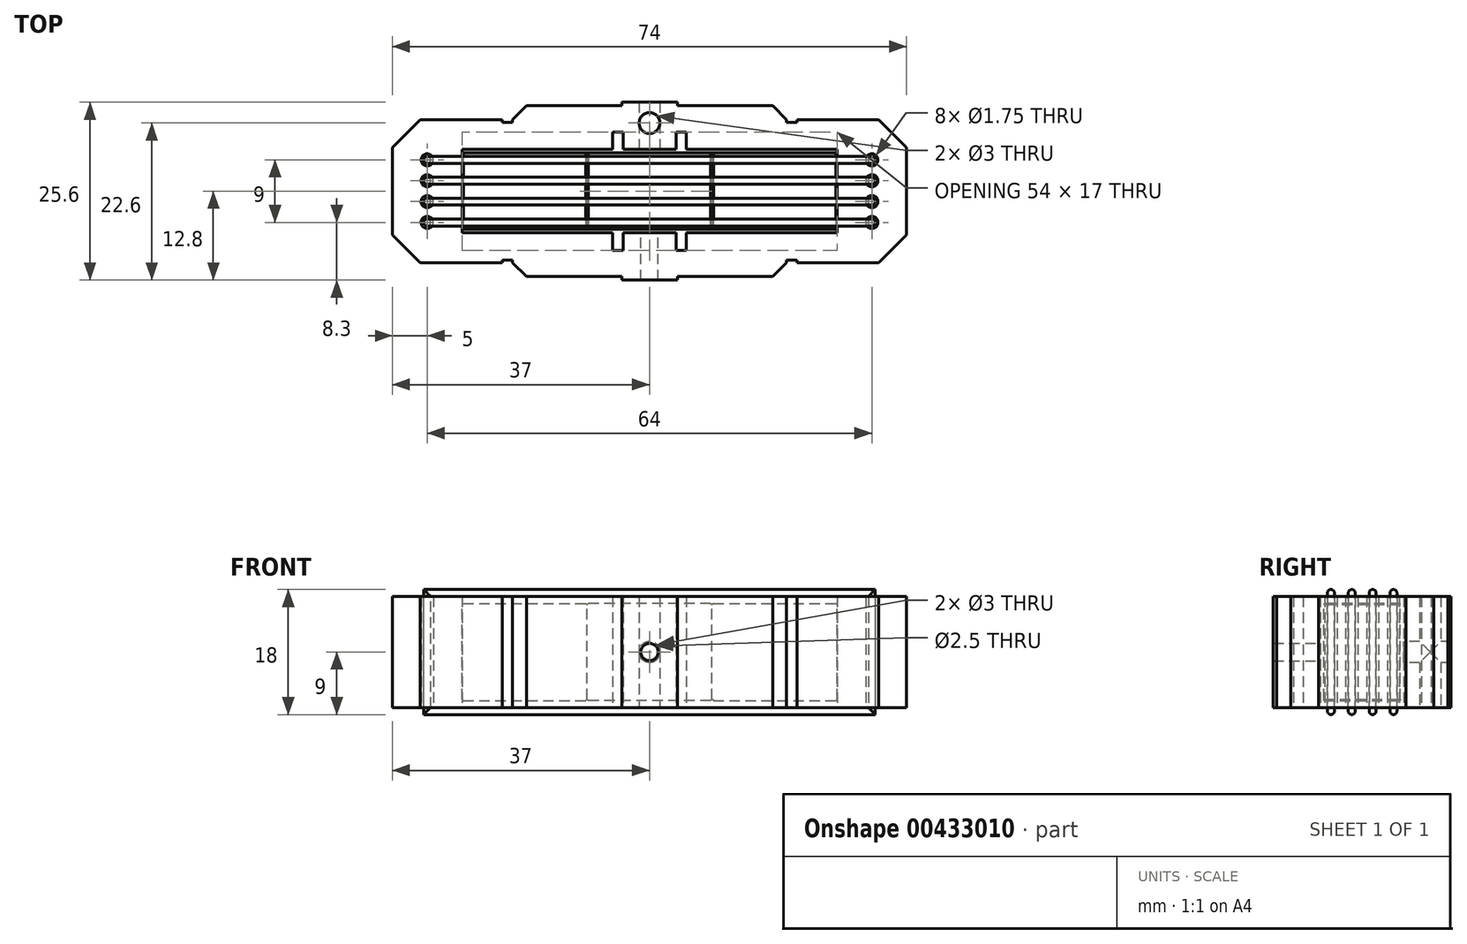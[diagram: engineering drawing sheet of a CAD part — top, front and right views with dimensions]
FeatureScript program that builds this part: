
annotation { "Feature Type Name" : "Feature", "Feature Type Description" : "" }
export const myFeature = defineFeature(function(context is Context, id is Id, definition is map)
    precondition{}
    {
        {
            var Q0;
            Q0=qCreatedBy(makeId("Top.planeOp"),FACE);
            var sketch = newSketch(context, id + "F0", { "sketchPlane" : qUnion([Q0])});
            skLineSegment(sketch, "E0", {"start": v(0, 12.8) * mm, "end": v(4, 12.8) * mm});
            skLineSegment(sketch, "E1", {"start": v(4, 12.8) * mm, "end": v(4, 12.3) * mm});
            skLineSegment(sketch, "E2", {"start": v(4, 12.3) * mm, "end": v(17.72, 12.3) * mm});
            skLineSegment(sketch, "E3", {"start": v(19.72, 9.92) * mm, "end": v(21.22, 9.92) * mm});
            skLineSegment(sketch, "E4", {"start": v(21.22, 9.92) * mm, "end": v(21.22, 10.3) * mm});
            skLineSegment(sketch, "E5", {"start": v(21.22, 10.3) * mm, "end": v(33, 10.3) * mm});
            skLineSegment(sketch, "E6", {"start": v(33, 10.3) * mm, "end": v(37, 6.3) * mm});
            skLineSegment(sketch, "E7", {"start": v(37, 6.3) * mm, "end": v(37, 0) * mm});
            skLineSegment(sketch, "E8", {"start": v(17.72, 12.3) * mm, "end": v(19.72, 10.3) * mm});
            skLineSegment(sketch, "E9", {"start": v(19.72, 10.3) * mm, "end": v(19.72, 9.92) * mm});
            skLineSegment(sketch, "E10", {"start": v(37, 0) * mm, "end": v(27, 0) * mm});
            skLineSegment(sketch, "E11", {"start": v(27, 0) * mm, "end": v(27, 6) * mm});
            skLineSegment(sketch, "E12", {"start": v(0, 6) * mm, "end": v(0, 12.8) * mm});
            skLineSegment(sketch, "E13", {"start": v(27, 6) * mm, "end": v(5.3, 6) * mm});
            skLineSegment(sketch, "E14", {"start": v(5.3, 6) * mm, "end": v(5.3, 8.5) * mm});
            skLineSegment(sketch, "E15", {"start": v(5.3, 8.5) * mm, "end": v(3.8, 8.5) * mm});
            skLineSegment(sketch, "E16", {"start": v(3.8, 8.5) * mm, "end": v(3.8, 6) * mm});
            skLineSegment(sketch, "E17", {"start": v(3.8, 6) * mm, "end": v(0, 6) * mm});
            skPoint(sketch, "E18", {"position": v(32, 4.5) * mm});
            skPoint(sketch, "E19", {"position": v(32, 1.5) * mm});
            skCircle(sketch, "E20", {"center": v(32, 1.5) * mm, "radius": 0.88 * mm});
            skCircle(sketch, "E21", {"center": v(32, 4.5) * mm, "radius": 0.88 * mm});
            skSolve(sketch);
        }
        {
            var Q0;
            Q0 = qSketchRegion(id + "F0", true);
            extrude(context, id + "F1", {"entities" : qUnion([Q0]), "depth" : 16 * mm, "symmetric" : true});
        }
        {
            var Q0;
            Q0=makeQuery(id+"F1.opExtrude","SWEPT_BODY",BODY,{"disambiguationData":[OSD([sQuery(id+"F0.wireOp",EDGE,"E0"),sQuery(id+"F0.wireOp",EDGE,"E1"),sQuery(id+"F0.wireOp",EDGE,"E2"),sQuery(id+"F0.wireOp",EDGE,"E3"),sQuery(id+"F0.wireOp",EDGE,"E4"),sQuery(id+"F0.wireOp",EDGE,"E5"),sQuery(id+"F0.wireOp",EDGE,"E6"),sQuery(id+"F0.wireOp",EDGE,"E7"),sQuery(id+"F0.wireOp",EDGE,"E8"),sQuery(id+"F0.wireOp",EDGE,"E9"),sQuery(id+"F0.wireOp",EDGE,"E10"),sQuery(id+"F0.wireOp",EDGE,"E11"),sQuery(id+"F0.wireOp",EDGE,"GGBhrQa4-wOD3-Jy7S-9Qvg-qyJeMn5F3UjZ"),sQuery(id+"F0.wireOp",EDGE,"E12")])]});
            var Q1;
            Q1=qCreatedBy(makeId("Front.planeOp"),FACE);
            mirror(context, id + "F2", {"operationType" : NewBodyOperationType.ADD, "entities" : qUnion([Q0]), "mirrorPlane" : qUnion([Q1])});
        }
        {
            var Q0;
            Q0=makeQuery(id+"F1.opExtrude","SWEPT_BODY",BODY,{"disambiguationData":[OSD([sQuery(id+"F0.wireOp",EDGE,"E0"),sQuery(id+"F0.wireOp",EDGE,"E1"),sQuery(id+"F0.wireOp",EDGE,"E2"),sQuery(id+"F0.wireOp",EDGE,"E3"),sQuery(id+"F0.wireOp",EDGE,"E4"),sQuery(id+"F0.wireOp",EDGE,"E5"),sQuery(id+"F0.wireOp",EDGE,"E6"),sQuery(id+"F0.wireOp",EDGE,"E7"),sQuery(id+"F0.wireOp",EDGE,"E8"),sQuery(id+"F0.wireOp",EDGE,"E9"),sQuery(id+"F0.wireOp",EDGE,"E10"),sQuery(id+"F0.wireOp",EDGE,"E11"),sQuery(id+"F0.wireOp",EDGE,"GGBhrQa4-wOD3-Jy7S-9Qvg-qyJeMn5F3UjZ"),sQuery(id+"F0.wireOp",EDGE,"E12")])]});
            var Q1;
            Q1=qCreatedBy(makeId("Right.planeOp"),FACE);
            mirror(context, id + "F3", {"operationType" : NewBodyOperationType.ADD, "entities" : qUnion([Q0]), "mirrorPlane" : qUnion([Q1])});
        }
        {
            var Q0;
            {var subQ0=makeQuery(id+"F1.opExtrude","CAP_FACE",FACE,{"disambiguationData":[OSD([sQuery(id+"F0.wireOp",EDGE,"E0"),sQuery(id+"F0.wireOp",EDGE,"E1"),sQuery(id+"F0.wireOp",EDGE,"E2"),sQuery(id+"F0.wireOp",EDGE,"E3"),sQuery(id+"F0.wireOp",EDGE,"E4"),sQuery(id+"F0.wireOp",EDGE,"E5"),sQuery(id+"F0.wireOp",EDGE,"E6"),sQuery(id+"F0.wireOp",EDGE,"E7"),sQuery(id+"F0.wireOp",EDGE,"E8"),sQuery(id+"F0.wireOp",EDGE,"E9"),sQuery(id+"F0.wireOp",EDGE,"E10"),sQuery(id+"F0.wireOp",EDGE,"E11"),sQuery(id+"F0.wireOp",EDGE,"E12"),sQuery(id+"F0.wireOp",EDGE,"E13"),sQuery(id+"F0.wireOp",EDGE,"E14"),sQuery(id+"F0.wireOp",EDGE,"E15"),sQuery(id+"F0.wireOp",EDGE,"E16"),sQuery(id+"F0.wireOp",EDGE,"E17")])],"isStart":false});var subQ1=makeQuery(id+"F2.boolean.opBoolean","MERGE",FACE,{"derivedFrom":[subQ0,makeQuery(id+"F2.opPattern","COPY",FACE,{"derivedFrom":subQ0,"instanceName":"1"})]});Q0=makeQuery(id+"F3.boolean.opBoolean","MERGE",FACE,{"derivedFrom":[subQ1,makeQuery(id+"F3.opPattern","COPY",FACE,{"derivedFrom":subQ1,"instanceName":"1"})]});}
            var sketch = newSketch(context, id + "F4", { "sketchPlane" : qUnion([Q0])});
            skPoint(sketch, "E22", {"position": v(0, 9.8) * mm});
            skSolve(sketch);
        }
        {
            var Q0;
            Q0=sQuery(id+"F4.wireOp",VERTEX,"E22");
            var Q1;
            Q1=makeQuery(id+"F1.opExtrude","SWEPT_BODY",BODY,{"disambiguationData":[OSD([sQuery(id+"F0.wireOp",EDGE,"E0"),sQuery(id+"F0.wireOp",EDGE,"E1"),sQuery(id+"F0.wireOp",EDGE,"E2"),sQuery(id+"F0.wireOp",EDGE,"E3"),sQuery(id+"F0.wireOp",EDGE,"E4"),sQuery(id+"F0.wireOp",EDGE,"E5"),sQuery(id+"F0.wireOp",EDGE,"E6"),sQuery(id+"F0.wireOp",EDGE,"E7"),sQuery(id+"F0.wireOp",EDGE,"E8"),sQuery(id+"F0.wireOp",EDGE,"E9"),sQuery(id+"F0.wireOp",EDGE,"E10"),sQuery(id+"F0.wireOp",EDGE,"E11"),sQuery(id+"F0.wireOp",EDGE,"E12"),sQuery(id+"F0.wireOp",EDGE,"E13"),sQuery(id+"F0.wireOp",EDGE,"E14"),sQuery(id+"F0.wireOp",EDGE,"E15"),sQuery(id+"F0.wireOp",EDGE,"E16"),sQuery(id+"F0.wireOp",EDGE,"E17")])]});
            hole(context, id + "F5", {"style" : HoleStyle.SIMPLE, "endStyle" : HoleEndStyle.THROUGH, "holeDiameter" : 3 * mm, "tappedDepth" : 12 * mm, "tapClearance" : 3, "locations" : qUnion([Q0]), "scope" : qUnion([Q1]), "startStyle" : HoleStartStyle.PART});
        }
        {
            var Q0;
            {var subQ0=makeQuery(id+"F2.opPattern","COPY",FACE,{"derivedFrom":makeQuery(id+"F1.opExtrude","SWEPT_FACE",FACE,{"disambiguationData":[OSD([sQuery(id+"F0.wireOp",EDGE,"E0")])]}),"instanceName":"1"});Q0=makeQuery(id+"F3.boolean.opBoolean","MERGE",FACE,{"derivedFrom":[subQ0,makeQuery(id+"F3.opPattern","COPY",FACE,{"derivedFrom":subQ0,"instanceName":"1"})]});}
            var sketch = newSketch(context, id + "F6", { "sketchPlane" : qUnion([Q0])});
            skPoint(sketch, "E23", {"position": v(0, 0) * mm});
            skSolve(sketch);
        }
        {
            var Q0;
            Q0=sQuery(id+"F6.wireOp",VERTEX,"E23");
            var Q1;
            Q1=makeQuery(id+"F1.opExtrude","SWEPT_BODY",BODY,{"disambiguationData":[OSD([sQuery(id+"F0.wireOp",EDGE,"E0"),sQuery(id+"F0.wireOp",EDGE,"E1"),sQuery(id+"F0.wireOp",EDGE,"E2"),sQuery(id+"F0.wireOp",EDGE,"E3"),sQuery(id+"F0.wireOp",EDGE,"E4"),sQuery(id+"F0.wireOp",EDGE,"E5"),sQuery(id+"F0.wireOp",EDGE,"E6"),sQuery(id+"F0.wireOp",EDGE,"E7"),sQuery(id+"F0.wireOp",EDGE,"E8"),sQuery(id+"F0.wireOp",EDGE,"E9"),sQuery(id+"F0.wireOp",EDGE,"E10"),sQuery(id+"F0.wireOp",EDGE,"E11"),sQuery(id+"F0.wireOp",EDGE,"E12"),sQuery(id+"F0.wireOp",EDGE,"E13"),sQuery(id+"F0.wireOp",EDGE,"E14"),sQuery(id+"F0.wireOp",EDGE,"E15"),sQuery(id+"F0.wireOp",EDGE,"E16"),sQuery(id+"F0.wireOp",EDGE,"E17"),sQuery(id+"F0.wireOp",EDGE,"E20"),sQuery(id+"F0.wireOp",EDGE,"E21")])]});
            hole(context, id + "F7", {"style" : HoleStyle.SIMPLE, "endStyle" : HoleEndStyle.BLIND, "standardTappedOrClearance" : lookupTablePath({ "standard" : "ISO", "engagement" : "75%", "pitch" : "0.5 mm", "size" : "M3", "type" : "Tapped" }), "standardBlindInLast" : lookupTablePath({ "standard" : "ISO", "engagement" : "75%", "pitch" : "0.5 mm", "size" : "M3", "type" : "Tapped" }), "holeDiameter" : 2.5 * mm, "showTappedDepth" : true, "holeDepth" : 13.5 * mm, "tappedDepth" : 12 * mm, "tapClearance" : 3, "locations" : qUnion([Q0]), "scope" : qUnion([Q1]), "majorDiameter" : 3 * mm, "startStyle" : HoleStartStyle.PART});
        }
        {
            var Q0;
            {var subQ0=makeQuery(id+"F1.opExtrude","SWEPT_FACE",FACE,{"disambiguationData":[OSD([sQuery(id+"F0.wireOp",EDGE,"E0")])]});Q0=makeQuery(id+"F3.boolean.opBoolean","MERGE",FACE,{"derivedFrom":[subQ0,makeQuery(id+"F3.opPattern","COPY",FACE,{"derivedFrom":subQ0,"instanceName":"1"})]});}
            var sketch = newSketch(context, id + "F8", { "sketchPlane" : qUnion([Q0])});
            skPoint(sketch, "E24", {"position": v(0, 0) * mm});
            skSolve(sketch);
        }
        {
            var Q0;
            Q0=sQuery(id+"F8.wireOp",VERTEX,"E24");
            var Q1;
            Q1=makeQuery(id+"F1.opExtrude","SWEPT_BODY",BODY,{"disambiguationData":[OSD([sQuery(id+"F0.wireOp",EDGE,"E0"),sQuery(id+"F0.wireOp",EDGE,"E1"),sQuery(id+"F0.wireOp",EDGE,"E2"),sQuery(id+"F0.wireOp",EDGE,"E3"),sQuery(id+"F0.wireOp",EDGE,"E4"),sQuery(id+"F0.wireOp",EDGE,"E5"),sQuery(id+"F0.wireOp",EDGE,"E6"),sQuery(id+"F0.wireOp",EDGE,"E7"),sQuery(id+"F0.wireOp",EDGE,"E8"),sQuery(id+"F0.wireOp",EDGE,"E9"),sQuery(id+"F0.wireOp",EDGE,"E10"),sQuery(id+"F0.wireOp",EDGE,"E11"),sQuery(id+"F0.wireOp",EDGE,"E12"),sQuery(id+"F0.wireOp",EDGE,"E13"),sQuery(id+"F0.wireOp",EDGE,"E14"),sQuery(id+"F0.wireOp",EDGE,"E15"),sQuery(id+"F0.wireOp",EDGE,"E16"),sQuery(id+"F0.wireOp",EDGE,"E17"),sQuery(id+"F0.wireOp",EDGE,"E20"),sQuery(id+"F0.wireOp",EDGE,"E21")])]});
            hole(context, id + "F9", {"style" : HoleStyle.SIMPLE, "endStyle" : HoleEndStyle.BLIND, "holeDiameter" : 3 * mm, "holeDepth" : 13.5 * mm, "tappedDepth" : 12 * mm, "tapClearance" : 3, "locations" : qUnion([Q0]), "scope" : qUnion([Q1]), "startStyle" : HoleStartStyle.PART});
        }
        {
            var Q0;
            Q0=qCreatedBy(makeId("Front.planeOp"),FACE);
            var sketch = newSketch(context, id + "F10", { "sketchPlane" : qUnion([Q0])});
            skLineSegment(sketch, "E25.bottom", {"start": v(32, -8.5) * mm, "end": v(-32, -8.5) * mm});
            skLineSegment(sketch, "E25.top", {"start": v(32, 8.5) * mm, "end": v(-32, 8.5) * mm});
            skLineSegment(sketch, "E25.left", {"start": v(32, -8.5) * mm, "end": v(32, 8.5) * mm});
            skLineSegment(sketch, "E25.right", {"start": v(-32, -8.5) * mm, "end": v(-32, 8.5) * mm});
            skPoint(sketch, "E25.middle", {"position": v(0, 0) * mm});
            skSolve(sketch);
        }
        {
            var Q0;
            Q0=qCreatedBy(makeId("Right.planeOp"),FACE);
            var sketch = newSketch(context, id + "F11", { "sketchPlane" : qUnion([Q0])});
            skPoint(sketch, "E26", {"position": v(-4.5, 8.5) * mm});
            skCircle(sketch, "E27", {"center": v(-4.5, 8.5) * mm, "radius": 0.5 * mm});
            skCircle(sketch, "E28.1.0.0", {"center": v(-1.5, 8.5) * mm, "radius": 0.5 * mm});
            skCircle(sketch, "E28.2.0.0", {"center": v(1.5, 8.5) * mm, "radius": 0.5 * mm});
            skCircle(sketch, "E28.3.0.0", {"center": v(4.5, 8.5) * mm, "radius": 0.5 * mm});
            skLineSegment(sketch, "E28.direction1", {"start": v(-4.5, 8.5) * mm, "end": v(-1.5, 8.5) * mm, "construction": true});
            skSolve(sketch);
        }
        {
            var Q0;
            Q0 = qSketchRegion(id + "F11", true);
            var Q1;
            Q1 = qConstructionFilter(qBodyType(qCreatedBy(id + "F10" ,EDGE), BodyType.WIRE), ConstructionObject.NO);
            sweep(context, id + "F12", {"profiles" : qUnion([Q0]), "path" : qUnion([Q1])});
        }
        {
            var Q0;
            Q0=qCreatedBy(makeId("Right.planeOp"),FACE);
            var sketch = newSketch(context, id + "F13", { "sketchPlane" : qUnion([Q0])});
            skLineSegment(sketch, "E29.bottom", {"start": v(-5.5, -7) * mm, "end": v(5.5, -7) * mm});
            skLineSegment(sketch, "E29.top", {"start": v(-5.5, 7) * mm, "end": v(5.5, 7) * mm});
            skLineSegment(sketch, "E29.left", {"start": v(-5.5, -7) * mm, "end": v(-5.5, 7) * mm});
            skLineSegment(sketch, "E29.right", {"start": v(5.5, -7) * mm, "end": v(5.5, 7) * mm});
            skPoint(sketch, "E29.middle", {"position": v(0, 0) * mm});
            skSolve(sketch);
        }
        {
            var Q0;
            Q0=makeQuery(id+"F13.imprint","IMPRINT",FACE,{"disambiguationData":[TD([[makeQuery(id+"F13.imprint","IMPRINT",EDGE,{"derivedFrom":sQuery(id+"F13.wireOp",EDGE,"E29.bottom")}),1.0]])]});
            extrude(context, id + "F14", {"entities" : qUnion([Q0]), "depth" : 18 * mm, "symmetric" : true});
        }
        {
            var Q0;
            Q0=makeQuery(id+"F14.opExtrude","CAP_EDGE",EDGE,{"disambiguationData":[OSD([sQuery(id+"F13.wireOp",EDGE,"E29.top")])],"isStart":false});
            var Q1;
            Q1=makeQuery(id+"F14.opExtrude","CAP_EDGE",EDGE,{"disambiguationData":[OSD([sQuery(id+"F13.wireOp",EDGE,"E29.top")])],"isStart":true});
            var Q2;
            Q2=makeQuery(id+"F14.opExtrude","CAP_EDGE",EDGE,{"disambiguationData":[OSD([sQuery(id+"F13.wireOp",EDGE,"E29.bottom")])],"isStart":false});
            var Q3;
            Q3=makeQuery(id+"F14.opExtrude","CAP_EDGE",EDGE,{"disambiguationData":[OSD([sQuery(id+"F13.wireOp",EDGE,"E29.bottom")])],"isStart":true});
            chamfer(context, id + "F15", {"entities" : qUnion([Q0, Q1, Q2, Q3]), "width" : 0.2 * mm, "tangentPropagation" : true});
        }
        {
            var Q0;
            Q0=makeQuery(id+"F14.opExtrude","SWEPT_BODY",BODY,{"disambiguationData":[OSD([sQuery(id+"F13.wireOp",EDGE,"E29.bottom"),sQuery(id+"F13.wireOp",EDGE,"E29.top"),sQuery(id+"F13.wireOp",EDGE,"E29.left"),sQuery(id+"F13.wireOp",EDGE,"E29.right")])]});
            var Q1;
            Q1=makeQuery(id+"F14.opExtrude","CAP_FACE",FACE,{"disambiguationData":[OSD([sQuery(id+"F13.wireOp",EDGE,"E29.bottom"),sQuery(id+"F13.wireOp",EDGE,"E29.top"),sQuery(id+"F13.wireOp",EDGE,"E29.left"),sQuery(id+"F13.wireOp",EDGE,"E29.right")])],"isStart":true});
            mirror(context, id + "F16", {"entities" : qUnion([Q0]), "mirrorPlane" : qUnion([Q1])});
        }
        {
            var Q0;
            Q0=makeQuery(id+"F14.opExtrude","SWEPT_BODY",BODY,{"disambiguationData":[OSD([sQuery(id+"F13.wireOp",EDGE,"E29.bottom"),sQuery(id+"F13.wireOp",EDGE,"E29.top"),sQuery(id+"F13.wireOp",EDGE,"E29.left"),sQuery(id+"F13.wireOp",EDGE,"E29.right")])]});
            var Q1;
            Q1=makeQuery(id+"F14.opExtrude","CAP_FACE",FACE,{"disambiguationData":[OSD([sQuery(id+"F13.wireOp",EDGE,"E29.bottom"),sQuery(id+"F13.wireOp",EDGE,"E29.top"),sQuery(id+"F13.wireOp",EDGE,"E29.left"),sQuery(id+"F13.wireOp",EDGE,"E29.right")])],"isStart":false});
            mirror(context, id + "F17", {"entities" : qUnion([Q0]), "mirrorPlane" : qUnion([Q1])});
        }
    });
